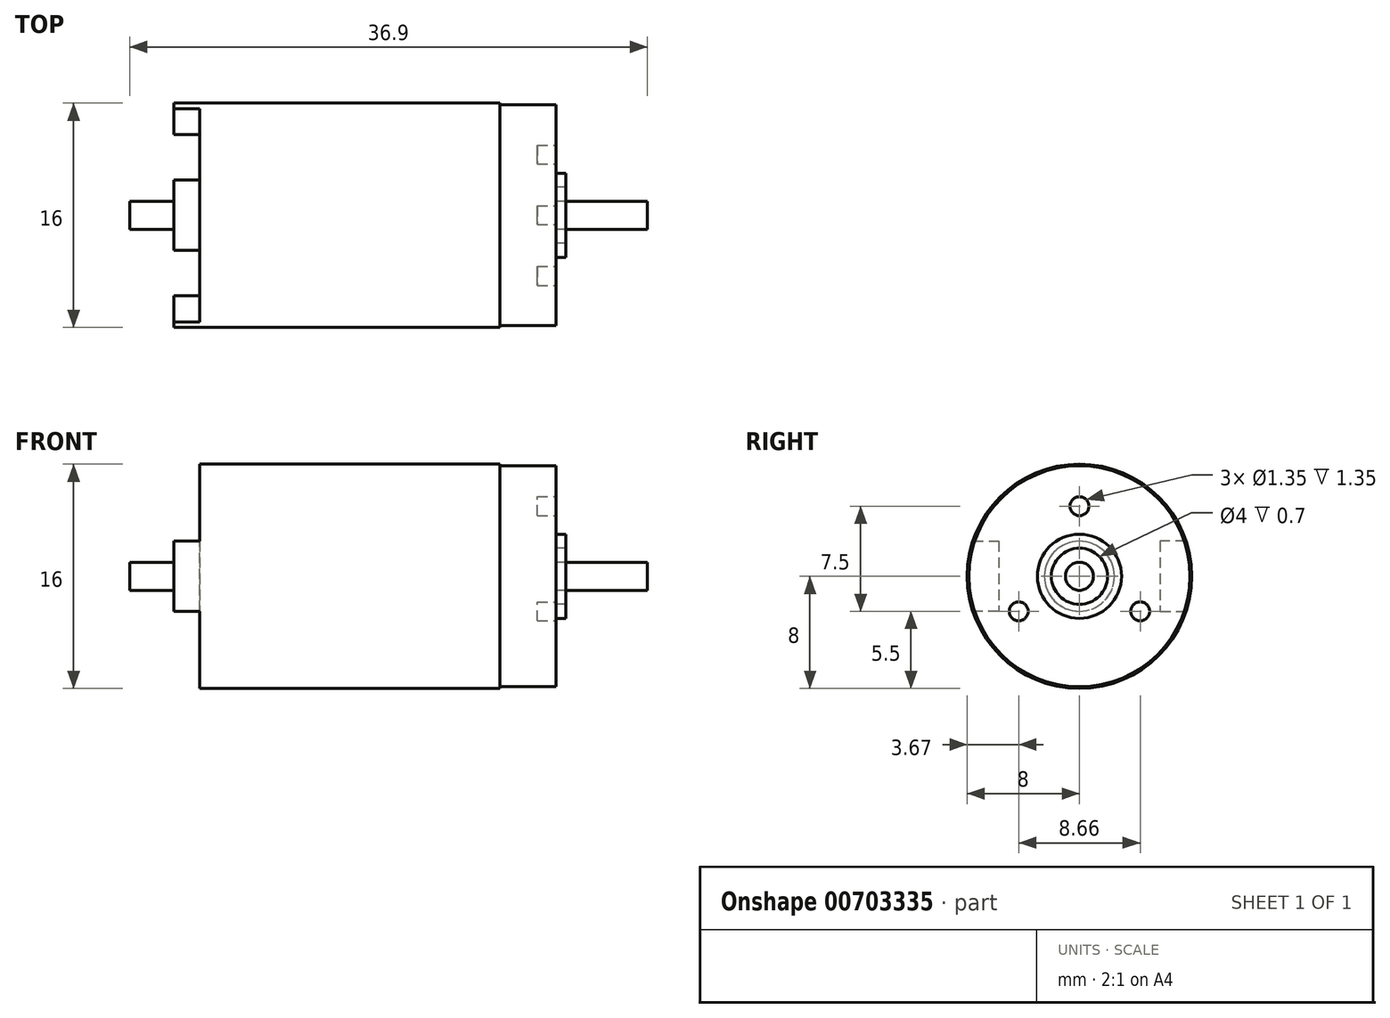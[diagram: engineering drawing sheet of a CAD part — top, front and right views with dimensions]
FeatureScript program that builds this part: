
annotation { "Feature Type Name" : "Feature", "Feature Type Description" : "" }
export const myFeature = defineFeature(function(context is Context, id is Id, definition is map)
    precondition{}
    {
        {
            var Q0;
            Q0=qCreatedBy(makeId("Right.planeOp"),FACE);
            var sketch = newSketch(context, id + "F0", { "sketchPlane" : qUnion([Q0])});
            skCircle(sketch, "E0", {"center": v(0, 0) * mm, "radius": 8 * mm});
            skCircle(sketch, "E1", {"center": v(0, 0) * mm, "radius": 3 * mm});
            skCircle(sketch, "E2", {"center": v(0, 0) * mm, "radius": 1 * mm});
            skCircle(sketch, "E3", {"center": v(0, 5) * mm, "radius": 0.68 * mm});
            skCircle(sketch, "E4", {"center": v(4.33, -2.5) * mm, "radius": 0.68 * mm});
            skCircle(sketch, "E5", {"center": v(-4.33, -2.5) * mm, "radius": 0.67 * mm});
            skCircle(sketch, "E6", {"center": v(0, 0) * mm, "radius": 2 * mm});
            skCircle(sketch, "E7", {"center": v(0, 0) * mm, "radius": 7.88 * mm});
            skSolve(sketch);
        }
        {
            var Q0;
            Q0=makeQuery(id+"F0.imprint","IMPRINT",FACE,{"disambiguationData":[TD([[makeQuery(id+"F0.imprint","IMPRINT",EDGE,{"derivedFrom":sQuery(id+"F0.wireOp",EDGE,"E0")}),1.0]])]});
            var Q1;
            Q1=makeQuery(id+"F0.imprint","IMPRINT",FACE,{"disambiguationData":[TD([[makeQuery(id+"F0.imprint","IMPRINT",EDGE,{"derivedFrom":sQuery(id+"F0.wireOp",EDGE,"E3")}),1.0]])]});
            var Q2;
            Q2=makeQuery(id+"F0.imprint","IMPRINT",FACE,{"disambiguationData":[TD([[makeQuery(id+"F0.imprint","IMPRINT",EDGE,{"derivedFrom":sQuery(id+"F0.wireOp",EDGE,"E4")}),1.0]])]});
            var Q3;
            Q3=makeQuery(id+"F0.imprint","IMPRINT",FACE,{"disambiguationData":[TD([[makeQuery(id+"F0.imprint","IMPRINT",EDGE,{"derivedFrom":sQuery(id+"F0.wireOp",EDGE,"E5")}),1.0]])]});
            var Q4;
            Q4=makeQuery(id+"F0.imprint","IMPRINT",FACE,{"disambiguationData":[TD([[makeQuery(id+"F0.imprint","IMPRINT",EDGE,{"derivedFrom":sQuery(id+"F0.wireOp",EDGE,"E2")}),1.0]])]});
            var Q5;
            Q5=makeQuery(id+"F0.imprint","IMPRINT",FACE,{"disambiguationData":[TD([[makeQuery(id+"F0.imprint","IMPRINT",EDGE,{"derivedFrom":sQuery(id+"F0.wireOp",EDGE,"E2")}),-1.0]])]});
            var Q6;
            Q6=makeQuery(id+"F0.imprint","IMPRINT",FACE,{"disambiguationData":[TD([[makeQuery(id+"F0.imprint","IMPRINT",EDGE,{"derivedFrom":sQuery(id+"F0.wireOp",EDGE,"E1")}),1.0]])]});
            var Q7;
            Q7=makeQuery(id+"F0.imprint","IMPRINT",FACE,{"disambiguationData":[TD([[makeQuery(id+"F0.imprint","IMPRINT",EDGE,{"derivedFrom":sQuery(id+"F0.wireOp",EDGE,"E1")}),-1.0]])]});
            extrude(context, id + "F1", {"entities" : qUnion([Q0, Q1, Q2, Q3, Q4, Q5, Q6, Q7]), "depth" : -25.4 * mm, "offsetDistance" : 25 * mm});
        }
        {
            var Q0;
            Q0=makeQuery(id+"F0.imprint","IMPRINT",FACE,{"disambiguationData":[TD([[makeQuery(id+"F0.imprint","IMPRINT",EDGE,{"derivedFrom":sQuery(id+"F0.wireOp",EDGE,"E2")}),1.0]])]});
            extrude(context, id + "F2", {"entities" : qUnion([Q0]), "operationType" : NewBodyOperationType.ADD, "depth" : 6.5 * mm, "offsetDistance" : 25 * mm});
        }
        {
            var Q0;
            Q0=makeQuery(id+"F0.imprint","IMPRINT",FACE,{"disambiguationData":[TD([[makeQuery(id+"F0.imprint","IMPRINT",EDGE,{"derivedFrom":sQuery(id+"F0.wireOp",EDGE,"E1")}),1.0]])]});
            extrude(context, id + "F3", {"entities" : qUnion([Q0]), "operationType" : NewBodyOperationType.ADD, "depth" : 0.7 * mm, "offsetDistance" : 25 * mm});
        }
        {
            var Q0;
            Q0=makeQuery(id+"F0.imprint","IMPRINT",FACE,{"disambiguationData":[TD([[makeQuery(id+"F0.imprint","IMPRINT",EDGE,{"derivedFrom":sQuery(id+"F0.wireOp",EDGE,"E3")}),1.0]])]});
            var Q1;
            Q1=makeQuery(id+"F0.imprint","IMPRINT",FACE,{"disambiguationData":[TD([[makeQuery(id+"F0.imprint","IMPRINT",EDGE,{"derivedFrom":sQuery(id+"F0.wireOp",EDGE,"E4")}),1.0]])]});
            var Q2;
            Q2=makeQuery(id+"F0.imprint","IMPRINT",FACE,{"disambiguationData":[TD([[makeQuery(id+"F0.imprint","IMPRINT",EDGE,{"derivedFrom":sQuery(id+"F0.wireOp",EDGE,"E5")}),1.0]])]});
            extrude(context, id + "F4", {"entities" : qUnion([Q0, Q1, Q2]), "operationType" : NewBodyOperationType.REMOVE, "depth" : -1.35 * mm, "offsetDistance" : 25 * mm});
        }
        {
            var Q0;
            Q0=makeQuery(id+"F0.imprint","IMPRINT",FACE,{"disambiguationData":[TD([[makeQuery(id+"F0.imprint","IMPRINT",EDGE,{"derivedFrom":sQuery(id+"F0.wireOp",EDGE,"E0")}),1.0]])]});
            extrude(context, id + "F5", {"entities" : qUnion([Q0]), "operationType" : NewBodyOperationType.REMOVE, "oppositeDirection" : true, "depth" : 4 * mm, "offsetDistance" : 25 * mm});
        }
        {
            var Q0;
            Q0=makeQuery(id+"F1.opExtrude","CAP_FACE",FACE,{"disambiguationData":[OSD([sQuery(id+"F0.wireOp",EDGE,"E0")])],"isStart":false});
            var sketch = newSketch(context, id + "F6", { "sketchPlane" : qUnion([Q0])});
            skCircle(sketch, "E8", {"center": v(0, 0) * mm, "radius": 2.5 * mm});
            skLineSegment(sketch, "E9", {"start": v(-7.6, 2.5) * mm, "end": v(-5.75, 2.5) * mm});
            skLineSegment(sketch, "E10", {"start": v(-5.75, 2.5) * mm, "end": v(-5.75, -2.5) * mm});
            skLineSegment(sketch, "E11", {"start": v(-5.75, -2.5) * mm, "end": v(-7.6, -2.5) * mm});
            skLineSegment(sketch, "E12", {"start": v(7.6, 2.5) * mm, "end": v(5.75, 2.5) * mm});
            skLineSegment(sketch, "E13", {"start": v(5.75, 2.5) * mm, "end": v(5.75, -2.5) * mm});
            skLineSegment(sketch, "E14", {"start": v(5.75, -2.5) * mm, "end": v(7.6, -2.5) * mm});
            skCircle(sketch, "E15", {"center": v(0, 0) * mm, "radius": 1 * mm});
            skSolve(sketch);
        }
        {
            var Q0;
            Q0=makeQuery(id+"F6.imprint","IMPRINT",FACE,{"disambiguationData":[TD([[makeQuery(id+"F6.imprint","IMPRINT",EDGE,{"derivedFrom":sQuery(id+"F6.wireOp",EDGE,"E15")}),1.0]])]});
            extrude(context, id + "F7", {"entities" : qUnion([Q0]), "operationType" : NewBodyOperationType.ADD, "depth" : 5 * mm, "offsetDistance" : 25 * mm});
        }
        {
            var Q0;
            Q0=makeQuery(id+"F6.imprint","IMPRINT",FACE,{"disambiguationData":[TD([[makeQuery(id+"F6.imprint","IMPRINT",EDGE,{"derivedFrom":sQuery(id+"F6.wireOp",EDGE,"E8")}),1.0]])]});
            var Q1;
            {var subQ0=sQuery(id+"F6.wireOp",EDGE,"E12");Q1=makeQuery(id+"F6.imprint","IMPRINT",FACE,{"disambiguationData":[TD([[makeQuery(id+"F6.imprint","IMPRINT",EDGE,{"derivedFrom":subQ0}),1.0]])]});}
            var Q2;
            {var subQ0=sQuery(id+"F6.wireOp",EDGE,"E9");Q2=makeQuery(id+"F6.imprint","IMPRINT",FACE,{"disambiguationData":[TD([[makeQuery(id+"F6.imprint","IMPRINT",EDGE,{"derivedFrom":subQ0}),-1.0]])]});}
            extrude(context, id + "F8", {"entities" : qUnion([Q0, Q1, Q2]), "operationType" : NewBodyOperationType.ADD, "depth" : 1.85 * mm, "offsetDistance" : 25 * mm});
        }
    });
